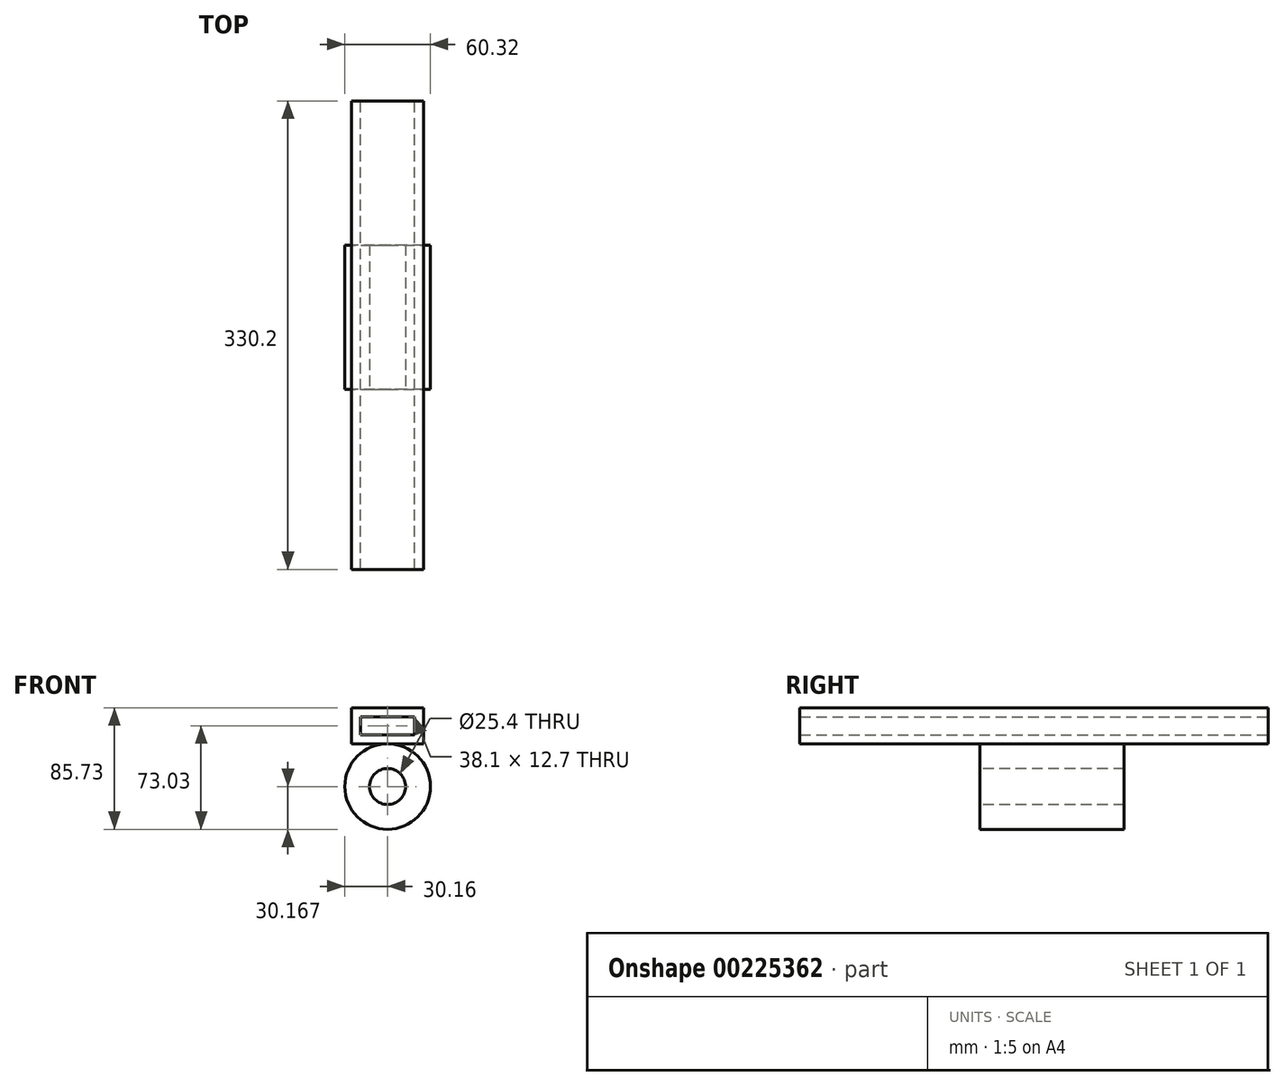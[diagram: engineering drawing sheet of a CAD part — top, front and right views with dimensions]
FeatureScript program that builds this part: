
annotation { "Feature Type Name" : "Feature", "Feature Type Description" : "" }
export const myFeature = defineFeature(function(context is Context, id is Id, definition is map)
    precondition{}
    {
        {
            var Q0;
            Q0=qCreatedBy(makeId("Front.planeOp"),FACE);
            var sketch = newSketch(context, id + "F0", { "sketchPlane" : qUnion([Q0])});
            skLineSegment(sketch, "E0", {"start": v(0, 0) * mm, "end": v(0, 25.4) * mm});
            skLineSegment(sketch, "E1", {"start": v(0, 25.4) * mm, "end": v(50.8, 25.4) * mm});
            skLineSegment(sketch, "E2", {"start": v(50.8, 25.4) * mm, "end": v(50.8, 0) * mm});
            skLineSegment(sketch, "E3", {"start": v(50.8, 0) * mm, "end": v(0, 0) * mm});
            skLineSegment(sketch, "E4.0", {"start": v(6.35, 6.35) * mm, "end": v(6.35, 19.05) * mm});
            skLineSegment(sketch, "E4.1", {"start": v(44.45, 6.35) * mm, "end": v(6.35, 6.35) * mm});
            skLineSegment(sketch, "E4.2", {"start": v(44.45, 19.05) * mm, "end": v(44.45, 6.35) * mm});
            skLineSegment(sketch, "E4.3", {"start": v(6.35, 19.05) * mm, "end": v(44.45, 19.05) * mm});
            skSolve(sketch);
        }
        {
            var Q0;
            Q0=makeQuery(id+"F0.imprint","IMPRINT",FACE,{"disambiguationData":[TD([[makeQuery(id+"F0.imprint","IMPRINT",EDGE,{"derivedFrom":sQuery(id+"F0.wireOp",EDGE,"E0")}),-1.0]])]});
            extrude(context, id + "F1", {"entities" : qUnion([Q0]), "depth" : 330.2 * mm});
        }
        {
            var Q0;
            Q0=makeQuery(id+"F1.opExtrude","CAP_FACE",FACE,{"disambiguationData":[OSD([sQuery(id+"F0.wireOp",EDGE,"E0"),sQuery(id+"F0.wireOp",EDGE,"E1"),sQuery(id+"F0.wireOp",EDGE,"E2"),sQuery(id+"F0.wireOp",EDGE,"E3"),sQuery(id+"F0.wireOp",EDGE,"E4.0"),sQuery(id+"F0.wireOp",EDGE,"E4.1"),sQuery(id+"F0.wireOp",EDGE,"E4.2"),sQuery(id+"F0.wireOp",EDGE,"E4.3")])],"isStart":false});
            var sketch = newSketch(context, id + "F2", { "sketchPlane" : qUnion([Q0])});
            skCircle(sketch, "E5", {"center": v(25.4, -30.16) * mm, "radius": 30.16 * mm});
            skPoint(sketch, "E5.centerSnap0", {"position": v(25.4, 0) * mm});
            skSolve(sketch);
        }
        {
            var Q0;
            Q0 = qSketchRegion(id + "F2", true);
            var Q1;
            Q1 = qSketchRegion(id + "F4", true);
            extrude(context, id + "F3", {"entities" : qUnion([Q0, Q1]), "operationType" : NewBodyOperationType.ADD, "oppositeDirection" : true, "depth" : 228.6 * mm});
        }
        {
            var Q0;
            Q0=makeQuery(id+"F3.opExtrude","CAP_FACE",FACE,{"disambiguationData":[OSD([sQuery(id+"F2.wireOp",EDGE,"E5")])],"isStart":true});
            var sketch = newSketch(context, id + "F4", { "sketchPlane" : qUnion([Q0])});
            skCircle(sketch, "E6", {"center": v(25.4, -30.16) * mm, "radius": 30.16 * mm});
            skSolve(sketch);
        }
        {
            var Q0;
            Q0 = qSketchRegion(id + "F4", true);
            extrude(context, id + "F5", {"entities" : qUnion([Q0]), "operationType" : NewBodyOperationType.REMOVE, "oppositeDirection" : true, "depth" : 127 * mm});
        }
        {
            var Q0;
            Q0=makeQuery(id+"F5.boolean.opBoolean","COPY",FACE,{"derivedFrom":makeQuery(id+"F5.opExtrude","CAP_FACE",FACE,{"disambiguationData":[OSD([sQuery(id+"F4.wireOp",EDGE,"E6")])],"isStart":false})});
            var sketch = newSketch(context, id + "F6", { "sketchPlane" : qUnion([Q0])});
            skCircle(sketch, "E7", {"center": v(25.4, -30.16) * mm, "radius": 12.7 * mm});
            skSolve(sketch);
        }
        {
            var Q0;
            Q0 = qSketchRegion(id + "F6", true);
            extrude(context, id + "F7", {"entities" : qUnion([Q0]), "operationType" : NewBodyOperationType.REMOVE, "endBound" : BoundingType.UP_TO_NEXT, "oppositeDirection" : true, "depth" : 25.4 * mm});
        }
    });
